# Revit family: STS-452 Контроллер_RV17_LOD400 (07.12.23)
name_source: partatom
category: Электрооборудование
revit_build: Autodesk Revit 2017 (Build: 20170118_1100(x64)
units: mm (PartAtom-declared; Revit-internal decimal feet)

## family parameters
Всегда вертикально = Нет
Конфигурация панели = Два столбца, слева направо
На основе рабочей плоскости = Да
Общий = Нет
При загрузке вырезать с полостями = Нет
Размер круглого соединителя = Использовать диаметр
Тип детали = Щит
Точка расчета площади = Нет

## types (1)
- STS-452
    ADSK_URL страницы изделия = https://stilsoft.ru
    ADSK_Единица измерения = шт.
    ADSK_Завод-изготовитель = ООО «Основа Безопасности»
    ADSK_Количество = 1
    ADSK_Марка = СТВФ.426469.019
    ADSK_Масса = 3
    ADSK_Наименование = Контроллер STS-452
    ADSK_Размер_Высота = 310 мм
    ADSK_Размер_Глубина = 80 мм
    ADSK_Размер_Длина = 180 мм
    d_короба = 20 мм
    Входное напряжение электропитания постоянного тока, номинальное, В = 48
    Входное напряжение электропитания постоянного тока, рабочий диапазон, В = 30…54
    Диапазон поддерживаемых скоростей по интерфейсу RS-485, Б/с = от 2400 до 115200
    Диапазон рабочих температур, °С = от –40 до +50
    Защита от импульсных помех и короткого замыкания выходного электропитания = Имеется
    Защита цепей Ethernet от импульсных перенапряжений = Имеется
    Информативность = 5
    Информационная ёмкость = 2
    Количество встроенных реле = 2
    Количество выходов типа «сухой контакт» = 2
    Количество подключаемых IP-видеокамер для устройств внутри цепи/ для конечных устройств в цепи = 1/2
    Количество портов Ethernet для организации сети связи = 2
    Количество портов RS-485 = 1
    Количество шлейфов сигнализации, шт. = 2
    Максимально допустимый потребляемый ток подключенного оборудования, А, при напряжении электропитания 24В = 2 А
    Максимально допустимый потребляемый ток подключенного оборудования, А, при напряжении электропитания 48В = 1 А
    Максимальное количество контроллеров в одной цепи, шт = 8
    Максимальное расстояние между соседними контроллерами, м = 100 мм
    Максимальный коммутируемый ток встроенного реле, А = 1 А
    Максимальный ток линии электропитания видеокамер, А = 1 А
    Максимальный ток линии электропитания извещателей, А = 1 А
    Напряжение = 24
    Отметка по умолчанию = 1219 мм
    Потребляемый ток (без учета подключенного оборудования), не более, А, при напряжении 48В = 0 А
    Потребляемый ток (без учета подключенного оборудования), не более, А, при напряжении 54В = 0 А
    Стандарт интерфейса связи = 10BaseT/100 BaseTХ Ethernet (RJ-45
